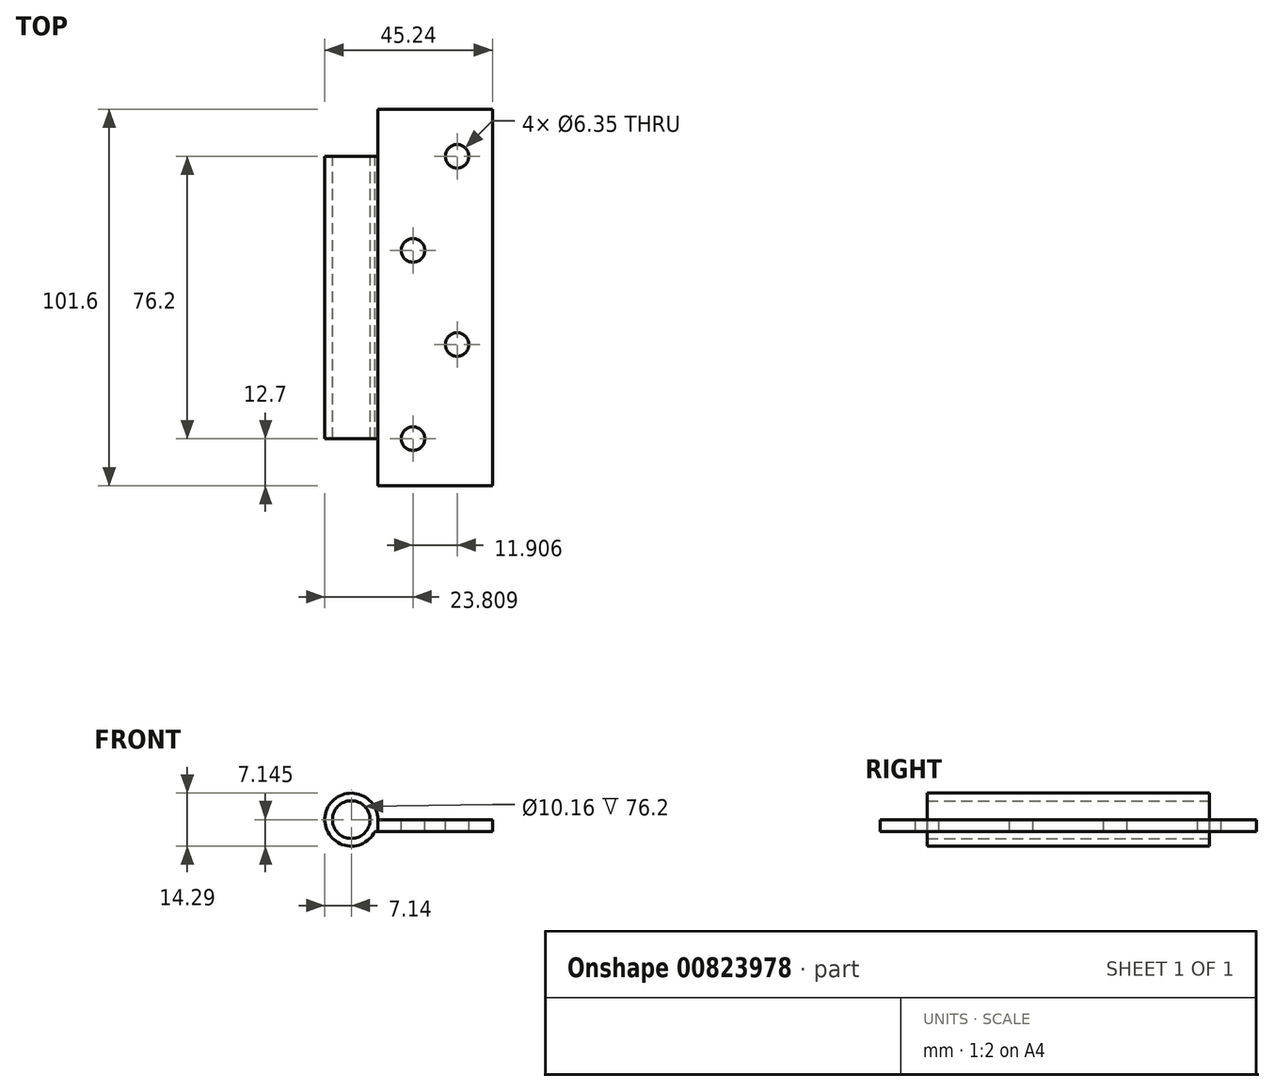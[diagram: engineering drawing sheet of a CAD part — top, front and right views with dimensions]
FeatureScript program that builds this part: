
annotation { "Feature Type Name" : "Feature", "Feature Type Description" : "" }
export const myFeature = defineFeature(function(context is Context, id is Id, definition is map)
    precondition{}
    {
        {
            var Q0;
            Q0=qCreatedBy(makeId("Front.planeOp"),FACE);
            var sketch = newSketch(context, id + "F0", { "sketchPlane" : qUnion([Q0])});
            skLineSegment(sketch, "E0.MirrorCS", {"start": v(7.14, 3.17) * mm, "end": v(38.1, 3.17) * mm});
            skLineSegment(sketch, "E1.MirrorCS", {"start": v(6.4, 0) * mm, "end": v(38.1, 0) * mm});
            skLineSegment(sketch, "E2.MirrorCS", {"start": v(38.1, 3.17) * mm, "end": v(38.1, 0) * mm});
            skCircle(sketch, "E3.MirrorC", {"center": v(0, 3.17) * mm, "radius": 7.14 * mm});
            skCircle(sketch, "E4.MirrorC", {"center": v(0, 3.17) * mm, "radius": 5.08 * mm});
            skLineSegment(sketch, "E5.MirrorCS", {"start": v(7.14, 3.17) * mm, "end": v(0, 3.17) * mm, "construction": true});
            skLineSegment(sketch, "E6.MirrorCS", {"start": v(0, 3.17) * mm, "end": v(0, 0) * mm, "construction": true});
            skLineSegment(sketch, "E7.MirrorCS", {"start": v(6.4, 0) * mm, "end": v(0, 0) * mm, "construction": true});
            skSolve(sketch);
        }
        {
            var Q0;
            Q0 = qSketchRegion(id + "F0", true);
            extrude(context, id + "F1", {"entities" : qUnion([Q0]), "endBound" : BoundingType.SYMMETRIC, "depth" : 101.6 * mm, "offsetDistance" : 25.4 * mm});
        }
        {
            var Q0;
            Q0=qCreatedBy(makeId("Top.planeOp"),FACE);
            var sketch = newSketch(context, id + "F2", { "sketchPlane" : qUnion([Q0])});
            skLineSegment(sketch, "E8.bottom", {"start": v(7.14, 38.1) * mm, "end": v(-7.26, 38.1) * mm});
            skLineSegment(sketch, "E8.top", {"start": v(7.14, 50.8) * mm, "end": v(-7.26, 50.8) * mm});
            skLineSegment(sketch, "E8.left", {"start": v(7.14, 38.1) * mm, "end": v(7.14, 50.8) * mm});
            skLineSegment(sketch, "E8.right", {"start": v(-7.26, 38.1) * mm, "end": v(-7.26, 50.8) * mm});
            skLineSegment(sketch, "E9.bottom", {"start": v(7.14, -38.1) * mm, "end": v(-7.26, -38.1) * mm});
            skLineSegment(sketch, "E9.top", {"start": v(7.14, -50.8) * mm, "end": v(-7.26, -50.8) * mm});
            skLineSegment(sketch, "E9.left", {"start": v(7.14, -38.1) * mm, "end": v(7.14, -50.8) * mm});
            skLineSegment(sketch, "E9.right", {"start": v(-7.26, -38.1) * mm, "end": v(-7.26, -50.8) * mm});
            skSolve(sketch);
        }
        {
            var Q0;
            Q0 = qSketchRegion(id + "F2", true);
            extrude(context, id + "F3", {"entities" : qUnion([Q0]), "operationType" : NewBodyOperationType.REMOVE, "endBound" : BoundingType.SYMMETRIC, "oppositeDirection" : true, "depth" : 25.4 * mm, "offsetDistance" : 25.4 * mm});
        }
        {
            var Q0;
            Q0=makeQuery(id+"F1.opExtrude","SWEPT_FACE",FACE,{"disambiguationData":[OSD([sQuery(id+"F0.wireOp",EDGE,"E0.MirrorCS")])]});
            var sketch = newSketch(context, id + "F4", { "sketchPlane" : qUnion([Q0])});
            skCircle(sketch, "E10", {"center": v(28.58, 38.1) * mm, "radius": 3.18 * mm});
            skCircle(sketch, "E11", {"center": v(28.58, -12.7) * mm, "radius": 3.18 * mm});
            skCircle(sketch, "E12", {"center": v(16.67, 12.7) * mm, "radius": 3.18 * mm});
            skCircle(sketch, "E13", {"center": v(16.67, -38.1) * mm, "radius": 3.18 * mm});
            skSolve(sketch);
        }
        {
            var Q0;
            Q0=sQuery(id+"F4.wireOp",VERTEX,"E10.center");
            var Q1;
            Q1=sQuery(id+"F4.wireOp",VERTEX,"E12.center");
            var Q2;
            Q2=sQuery(id+"F4.wireOp",VERTEX,"E11.center");
            var Q3;
            Q3=sQuery(id+"F4.wireOp",VERTEX,"E13.center");
            var Q4;
            Q4=makeQuery(id+"F1.opExtrude","SWEPT_BODY",BODY,{"disambiguationData":[OSD([sQuery(id+"F0.wireOp",EDGE,"E0.MirrorCS"),sQuery(id+"F0.wireOp",EDGE,"E1.MirrorCS"),sQuery(id+"F0.wireOp",EDGE,"E2.MirrorCS"),sQuery(id+"F0.wireOp",EDGE,"E3.MirrorC"),sQuery(id+"F0.wireOp",EDGE,"E4.MirrorC")])]});
            hole(context, id + "F5", {"style" : HoleStyle.SIMPLE, "endStyle" : HoleEndStyle.THROUGH, "holeDiameter" : 6.35 * mm, "majorDiameter" : 6.35 * mm, "isTappedThrough" : true, "tappedDepth" : 12.7 * mm, "tapClearance" : 3, "locations" : qUnion([Q0, Q1, Q2, Q3]), "scope" : qUnion([Q4])});
        }
    });
